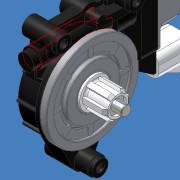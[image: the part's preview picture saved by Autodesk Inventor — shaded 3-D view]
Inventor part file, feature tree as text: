
AUTODESK INVENTOR PART (.ipt)
format: ipt  version: 2012 (Build 160160000, 160)  size: 1,703,424 bytes
history: native  units: mm (DEFAULTED — no unit token found)
features: sketch x58, extrude x51, fillet x10, chamfer x9, hole x6, pattern_circular x4, plane x2, revolve x1, other x1, mirror x1, projected_geometry x1
ambient origin geometry x8: Origin, YZ Plane, XZ Plane, XY Plane, X Axis, Y Axis, Z Axis, Center Point
bodies: Solid1 (feature_tree)
feature tree (144):
  extrude  "Extrusion1"  Depth=5.8mm TaperAngle=0.0deg
  extrude  "Extrusion2"  Depth=42.0mm
  extrude  "Extrusion3"  Depth=2.0mm
  extrude  "Extrusion4"  Depth=26.0mm
  extrude  "Extrusion5"  Depth=4.0mm
  pattern_circular  "Circular Pattern1"  Count=8 Angle=360.0deg
  extrude  "Extrusion6"  Depth=1.7mm TaperAngle=0.0deg
  extrude  "Extrusion7"  Depth=17.9mm TaperAngle=0.0deg
  hole  "Hole1"  [1 undecoded]
  extrude  "Extrusion8"  Depth=18.0mm TaperAngle=0.0deg
  chamfer  "Chamfer1"  Distance=2.0mm
  pattern_circular  "Circular Pattern2"  Count=6 Angle=360.0deg
  extrude  "Extrusion9"  Depth=0.2mm TaperAngle=0.0deg
  extrude  "Extrusion10"  Depth=8.2mm TaperAngle=0.0deg
  chamfer  "Chamfer2"  Distance=0.5mm
  fillet  "Fillet1"  Radius=0.5mm
  fillet  "Fillet2"  Radius=1.5mm
  extrude  "Extrusion11"  Depth=0.5mm TaperAngle=0.0deg
  extrude  "Extrusion12"  Depth=68.0mm
  extrude  "Extrusion13"  Depth=2.0mm
  revolve  "Revolution1"  [1 undecoded]
  extrude  "Extrusion14"  TaperAngle=30.0deg  [1 undecoded]
  pattern_circular  "Circular Pattern3"  Count=12 Angle=360.0deg
  extrude  "Extrusion15"  Depth=0.5mm
  fillet  "Fillet3"  Radius=43.0mm
  extrude  "Extrusion16"  Depth=2.0mm TaperAngle=0.0deg
  fillet  "Fillet4"  Radius=1.0mm
  hole  "Hole2"  [1 undecoded]
  extrude  "Extrusion18"  Depth=0.9mm
  fillet  "Fillet5"  Radius=120.0mm
  pattern_circular  "Circular Pattern4"  Count=2  [1 undecoded]
  plane  "Work Plane1"
  plane  "Work Plane2"
  other  "Work Axis1"
  extrude  "Extrusion19"  Depth=23.0mm
  extrude  "Extrusion20"  Depth=5.0mm TaperAngle=0.0deg
  extrude  "Extrusion21"  Depth=31.0mm
  extrude  "Extrusion22"  Depth=4.0mm
  extrude  "Extrusion23"  Depth=6.0mm
  fillet  "Fillet6"  Radius=2.0mm
  chamfer  "Chamfer3"  Distance=40.0mm
  chamfer  "Chamfer4"  Distance=35.0mm
  extrude  "Extrusion24"  Depth=1.0mm
  fillet  "Fillet7"  Radius=4.0mm
  extrude  "Extrusion25"  Depth=10.0mm
  extrude  "Extrusion26"  Depth=9.0mm
  chamfer  "Chamfer5"  Distance=5.0mm
  chamfer  "Chamfer6"  Distance=2.0mm
  fillet  "Fillet8"  Radius=13.2mm
  extrude  "Extrusion27"  Depth=18.0mm TaperAngle=0.0deg
  mirror  "Mirror1"
  extrude  "Extrusion28"  Depth=7.0mm
  extrude  "Extrusion29"  Depth=14.0mm
  fillet  "Fillet10"  Radius=8.2mm
  extrude  "Extrusion30"  Depth=3.0mm TaperAngle=0.0deg
  extrude  "Extrusion31"  Depth=2.0mm TaperAngle=0.0deg
  chamfer  "Chamfer8"  Distance=7.0mm
  extrude  "Extrusion32"  Depth=12.3mm
  extrude  "Extrusion33"  Depth=8.0mm TaperAngle=0.0deg
  extrude  "Extrusion34"  Depth=15.5mm
  hole  "Hole3"  [1 undecoded]
  extrude  "Extrusion35"  Depth=14.2mm
  extrude  "Extrusion36"  Depth=14.8mm TaperAngle=0.0deg
  extrude  "Extrusion39"  Depth=3.0mm TaperAngle=0.0deg
  extrude  "Extrusion40"  Depth=17.5mm TaperAngle=0.0deg
  extrude  "Extrusion41"  Depth=2.0mm TaperAngle=0.0deg
  hole  "Hole4"  [1 undecoded]
  extrude  "Extrusion42"  Depth=9.0mm
  extrude  "Extrusion43"  Depth=27.3mm TaperAngle=0.0deg
  extrude  "Extrusion46"  Depth=5.0mm
  extrude  "Extrusion47"  Depth=1.6mm
  extrude  "Extrusion48"  Depth=24.3mm TaperAngle=0.0deg
  hole  "Hole5"  [1 undecoded]
  hole  "Hole6"  [1 undecoded]
  extrude  "Extrusion50"  Depth=9.0mm
  extrude  "Extrusion51"  Depth=2.0mm
  extrude  "Extrusion52"  Depth=12.5mm TaperAngle=0.0deg
  extrude  "Extrusion53"  Depth=4.0mm
  chamfer  "Chamfer9"  Distance=22.68928mm
  extrude  "Extrusion55"  Depth=2.0mm
  fillet  "Fillet12"  Radius=2.0mm
  extrude  "Extrusion56"  Depth=56.58mm
  extrude  "Extrusion57"  Depth=41.0mm
  chamfer  "Chamfer10"  Distance=5.0mm
  extrude  "Extrusion59"  Depth=3.5mm
  sketch  "Sketch1"  dims[d0=72.0mm d1=5.8mm d2=0.0mm]
  sketch  "Sketch2"  dims[d3=60.0mm d4=42.0mm]
  sketch  "Sketch3"  dims[d5=2.0mm d6=0.0mm d7=2.0mm]
  sketch  "Sketch4"  dims[d8=1.0mm d9=0.0mm d10=26.0mm]
  sketch  "Sketch5"  dims[d11=0.5mm d12=0.0mm d13=4.0mm]
  sketch  "Sketch6"  dims[d14=8.0mm]
  sketch  "Sketch7"  dims[d15=22.0mm]
  sketch  "Sketch8"  dims[d16=1.5mm d17=0.0mm]
  sketch  "Sketch9"  dims[d18=2.0mm d19=80.0mm d21=360.0deg]
  sketch  "Sketch10"  dims[d22=23.9mm d23=1.7mm d24=0.0mm]
  sketch  "Sketch11"  dims[d25=16.2mm d26=17.9mm d27=0.0mm]
  sketch  "Sketch12"  dims[d28=13.0mm d29=6.0mm d30=4.0mm d31=2.0mm d32=14.3117mm d33=2.0mm d34=0.0mm d35=4.0mm]
  sketch  "Sketch13"  dims[d36=10.0mm d37=18.0mm d38=0.0mm d39=2.0mm d40=2.0mm d41=60.0mm d43=360.0deg]
  sketch  "Sketch14"  dims[d44=12.5mm d45=0.2mm d46=0.0mm]
  sketch  "Sketch15"  dims[d47=8.0mm d48=8.2mm d49=0.0mm d50=0.5mm d51=2.0mm d52=0.5mm d53=1.5mm]
  sketch  "Sketch16"  dims[d54=71.0mm d55=0.5mm d56=0.0mm]
  sketch  "Sketch17"  dims[d57=3.0mm d58=0.0mm d59=68.0mm]
  sketch  "Sketch18"  dims[d60=14.0mm d61=0.0mm d62=2.0mm]
  sketch  "Sketch19"  dims[d63=3.5mm d64=10.0mm]
  sketch  "Sketch21"  dims[d65=90.0deg d66=30.0deg]
  sketch  "Sketch22"  dims[d67=1.0mm]
  sketch  "Sketch23"  dims[d68=1.0mm]
  sketch  "Sketch24"  dims[d69=4.5mm d70=0.0mm d71=120.0mm d73=360.0deg]
  sketch  "Sketch25"  dims[d74=0.5mm d75=0.0mm d76=0.5mm d77=43.0mm]
  sketch  "Sketch26"  dims[d78=2.0mm d79=2.0mm d80=0.0mm d81=1.0mm]
  sketch  "Sketch27"  dims[d82=2.6mm d83=6.0mm d84=4.0mm d85=2.0mm d86=14.3117mm d87=8.0mm d88=0.0mm d93=2.0mm]
  sketch  "Sketch28"  dims[d94=15.5mm d95=0.0mm d96=0.9mm d97=120.0mm d99=360.0deg]
  sketch  "Sketch29"  dims[d100=-12.0mm d101=-33.88mm]
  sketch  "Sketch31"  dims[d102=15.0mm]
  sketch  "Sketch32"  dims[d103=35.0mm d104=0.0mm d105=20.0mm d106=0.0mm]
  sketch  "Sketch33"  dims[d108=14.5mm d109=0.0mm d110=23.0mm]
  sketch  "Sketch35"  dims[d111=12.25mm d112=5.0mm d113=0.0mm]
  sketch  "Sketch36"  dims[d114=60.0mm d115=31.0mm]
  sketch  "Sketch37"  dims[d116=12.5mm d117=0.0mm d118=4.0mm]
  sketch  "Sketch38"  dims[d119=12.0mm d120=6.0mm d121=6.0mm d122=12.0mm d127=2.0mm d128=0.0mm]
  sketch  "Sketch39"  dims[d129=1.0mm d130=40.0mm d131=15.0mm d132=0.0mm d133=35.0mm d135=40.0mm d136=0.0mm]
  sketch  "Sketch40"  dims[d137=2.5mm d138=12.0mm d139=1.0mm d140=12.0mm d143=4.0mm]
  sketch  "Sketch41"  dims[d145=43.0mm d146=0.0mm d150=10.0mm]
  sketch  "Sketch43"  dims[d151=4.0mm d152=0.0mm d153=9.0mm d154=5.0mm d155=0.0mm]
  sketch  "Sketch46"  dims[d156=1.0mm]
  sketch  "Sketch47"  dims[d157=0.5mm d158=2.0mm d159=0.0mm d160=13.2mm]
  sketch  "Sketch48"  dims[d161=30.0mm d162=18.0mm d163=0.0mm]
  sketch  "Sketch49"  dims[d164=9.0mm d165=14.0mm d166=7.0mm]
  sketch  "Sketch50"  dims[d167=50.0mm d168=0.0mm d170=14.0mm d172=8.2mm d173=0.0mm]
  sketch  "Sketch51"  dims[d174=12.3mm d175=3.0mm d176=0.0mm]
  sketch  "Sketch54"  dims[d177=4.8mm d178=6.0mm d179=6.2mm d180=2.0mm d181=14.3117mm d182=8.0mm d183=0.0mm d186=2.0mm d187=0.0mm d191=7.0mm d192=0.0mm]
  sketch  "Sketch55"  dims[d200=14.8mm d201=0.0mm d202=12.3mm]
  sketch  "Sketch56"  dims[d203=3.0mm d204=0.0mm d205=8.0mm d206=0.0mm]
  sketch  "Sketch57"  dims[d207=4.8mm d208=6.0mm d209=6.2mm d210=2.0mm d211=14.3117mm d212=8.0mm d213=0.0mm d214=15.5mm]
  sketch  "Sketch58"  dims[d217=16.0mm d218=0.0mm d219=9.0mm]
  sketch  "Sketch60"  dims[d222=9.5mm d223=0.0mm d230=14.2mm]
  sketch  "Sketch61"  dims[d231=48.4mm d232=14.8mm d233=0.0mm]
  sketch  "Sketch63"  dims[d234=12.3mm d235=3.0mm d236=0.0mm]
  sketch  "Sketch66"  dims[d237=16.5mm d238=17.5mm d239=0.0mm]
  sketch  "Sketch68"  dims[d240=4.8mm d241=6.0mm d242=6.2mm d243=2.0mm d244=14.3117mm d245=28.0mm d246=20.594885mm]
  sketch  "Sketch69"  dims[d247=4.134mm d248=6.0mm d249=4.9mm d250=2.0mm d251=14.3117mm d252=8.0mm d253=0.0mm d259=2.0mm d260=0.0mm]
  sketch  "Sketch70"  dims[d261=2.0mm d262=0.0mm d263=13.0mm d264=0.0mm]
  sketch  "Sketch72"  dims[d270=18.5mm d271=0.0mm d272=9.0mm d273=13.0mm d287=27.3mm d288=0.0mm d289=5.0mm d290=1.6mm d291=24.3mm d292=0.0mm d295=7.0mm d296=0.0mm d302=5.0mm d303=10.0mm d304=9.0mm d305=2.0mm d306=12.5mm d307=0.0mm d314=4.0mm d315=22.68928mm d317=2.0mm d318=2.0mm d320=56.58mm d321=41.0mm d322=5.0mm d324=3.5mm d327=120.0deg d328=0.2mm d329=0.2mm d330=0.2mm d332=20.0mm d333=34.340198mm d334=17.5mm d337=20.71mm d338=2.0mm d339=15.0mm d340=19.0mm d345=7.5mm d346=15.5mm d347=23.0mm d348=3.0mm d349=13.8mm d350=8.0mm d351=12.0mm d352=90.0deg d353=14.88mm d354=45.0deg d355=45.0deg d356=45.0deg d357=45.0deg d358=45.0deg d359=45.0deg d360=45.0deg d361=45.0deg d362=45.0deg]
  projected_geometry  "Projected Loop3"
note: 9 required parameter values undecoded (feature->parameter linkage not recoverable at this tier; creation-order binding heuristic only, values carry confidence <= 0.55)